# Revit family: 33-00-011-DN80-300
name_source: partatom
category: Pipe Accessories
units: mm (PartAtom-declared; Revit-internal decimal feet)

## family parameters
Always vertical = No
Cut with Voids When Loaded = No
Part Type = Valve - Breaks Into
Round Connector Dimension = Use Diameter
Shared = No
Work Plane-Based = No

## types (6) — shared parameters
Body_Wallthickness = 15 mm  [stored 0.0492126 ft]
Body_Wallthickness_ref = 8 mm  [stored 0.0262467 ft]
DN080_PN16 = 33-080-00-0147099
DN100_PN16 = 33-100-00-0147099
DN150_PN16 = 33-150-00-0147099
DN200_PN16 = 33-200-00-0147099
DN250_PN16 = 33-250-00-01770
DN300_PN16 = 33-300-00-01770
Description_ = AVK GATE VALVE WITH SOCKET ENDS
Ftc = 4 mm  [stored 0.0131234 ft]
Name_Height_reference = 10 mm  [stored 0.0328084 ft]
Rib_Thickness = 18 mm  [stored 0.0590551 ft]
Search_table = 33-00-011-DN80-300
URL product pages = https://www.avkvalves.com
zero-valued in all types: Bottom_Reference

## per-type parameters (varying)
- DN080_PN16: At=70 mm; Body_Height=130 mm; Body_depth=140 mm; Body_width=60 mm  [stored 0.19685 ft]; Bonnet_Flange_Depth=171 mm; Bonnet_Flange_Width=65 mm; Bonnet_Flange_cut=8 mm  [stored 0.0262467 ft]; Bonnet_Flange_thickness=15 mm  [stored 0.0492126 ft]; Bonnet_Height=50 mm  [stored 0.164042 ft]; Bonnet_Reference_height=120 mm; Bonnet_Thickness=61 mm; Bt=61 mm; Bt_2=54 mm  [stored 0.177165 ft]; CL _Thickness=19 mm  [stored 0.062336 ft]; CL_Height=75 mm; Cut_Reference=568 mm; D=63 mm; D1=10 mm  [stored 0.0328084 ft]; D2=34 mm  [stored 0.111549 ft]; Dd=98 mm; Dd_ref=49 mm  [stored 0.160761 ft]; F=9 mm; F1=20 mm  [stored 0.0656168 ft]; Fillet_Thickness=6 mm  [stored 0.019685 ft]; Flange_OR=100 mm; Flange_Thickness=30 mm  [stored 0.0984252 ft]; Flange_Thickness_cut=30 mm  [stored 0.0984252 ft]; Ftc_reference_height=100 mm; H=280 mm; H1=246 mm; H3=351 mm; H3_ref=71 mm; Horizontal_Flange_width=142 mm; ID=40 mm  [stored 0.131234 ft]; ID_ref=48 mm  [stored 0.15748 ft]; ID_ref_2=64 mm; L=284 mm; L_Dia=80 mm; L_ref=123 mm; Name_Reference=90 mm; Name_Width=30 mm  [stored 0.0984252 ft]; Neck_H=41 mm; Neck_T=17 mm  [stored 0.0557743 ft]; Neck_T2=15 mm  [stored 0.0492126 ft]; Nominal Diameter (DN)=80 mm; R1tv=1000 mm; R2f=15 mm  [stored 0.0492126 ft]; RF_Dia=66 mm; Rf=237 mm; Rib_Height_Reference_1=120 mm; Rib_Height_Reference_2=110 mm; Rib_Height_Reference_3=100 mm; Rib_Height_Reference_4=85 mm; Rib_Width_1=30 mm  [stored 0.0984252 ft]; Rib_Width_2=30 mm  [stored 0.0984252 ft]; Rib_Width_3=30 mm  [stored 0.0984252 ft]; Rib_depth_1=30 mm  [stored 0.0984252 ft]; Rib_depth_2=30 mm  [stored 0.0984252 ft]; Rib_depth_3=30 mm  [stored 0.0984252 ft]; Rt=333 mm
- DN100_PN16: At=83 mm; Body_Height=122 mm; Body_depth=166 mm; Body_width=65 mm; Bonnet_Flange_Depth=192 mm; Bonnet_Flange_Width=70 mm; Bonnet_Flange_cut=8 mm  [stored 0.0262467 ft]; Bonnet_Flange_thickness=15 mm  [stored 0.0492126 ft]; Bonnet_Height=55 mm  [stored 0.180446 ft]; Bonnet_Reference_height=112 mm; Bonnet_Thickness=66 mm; Bt=66 mm; Bt_2=59 mm; CL _Thickness=22 mm  [stored 0.0721785 ft]; CL_Height=88 mm; Cut_Reference=568 mm; D=63 mm; D1=10 mm  [stored 0.0328084 ft]; D2=34 mm  [stored 0.111549 ft]; Dd=118 mm; Dd_ref=59 mm; F=9 mm; F1=20 mm  [stored 0.0656168 ft]; Fillet_Thickness=6 mm  [stored 0.019685 ft]; Flange_OR=110 mm; Flange_Thickness=30 mm  [stored 0.0984252 ft]; Flange_Thickness_cut=30 mm  [stored 0.0984252 ft]; Ftc_reference_height=110 mm; H=303 mm; H1=269 mm; H3=384 mm; H3_ref=81 mm; Horizontal_Flange_width=162 mm; ID=50 mm  [stored 0.164042 ft]; ID_ref=58 mm; ID_ref_2=74 mm; L=284 mm; L_Dia=100 mm; L_ref=123 mm; Name_Reference=101 mm; Name_Width=33 mm; Neck_H=59 mm; Neck_T=20 mm  [stored 0.0656168 ft]; Neck_T2=18 mm  [stored 0.0590551 ft]; Nominal Diameter (DN)=100 mm; R1tv=1100 mm; R2f=15 mm  [stored 0.0492126 ft]; RF_Dia=78 mm; Rf=270 mm; Rib_Height_Reference_1=120 mm; Rib_Height_Reference_2=110 mm; Rib_Height_Reference_3=100 mm; Rib_Height_Reference_4=90 mm; Rib_Width_1=33 mm; Rib_Width_2=33 mm; Rib_Width_3=33 mm; Rib_depth_1=33 mm; Rib_depth_2=33 mm; Rib_depth_3=33 mm; Rt=367 mm
- DN150_PN16: At=121 mm; Body_Height=192 mm; Body_depth=242 mm; Body_width=75 mm; Bonnet_Flange_Depth=272 mm; Bonnet_Flange_Width=90 mm; Bonnet_Flange_cut=8 mm  [stored 0.0262467 ft]; Bonnet_Flange_thickness=15 mm  [stored 0.0492126 ft]; Bonnet_Height=71 mm; Bonnet_Reference_height=182 mm; Bonnet_Thickness=77 mm; Bt=77 mm; Bt_2=69 mm; CL _Thickness=24 mm  [stored 0.0787402 ft]; CL_Height=126 mm; Cut_Reference=568 mm; D=63 mm; D1=10 mm  [stored 0.0328084 ft]; D2=34 mm  [stored 0.111549 ft]; Dd=170 mm; Dd_ref=85 mm; F=9 mm; F1=20 mm  [stored 0.0656168 ft]; Fillet_Thickness=12 mm  [stored 0.0393701 ft]; Flange_OR=142 mm; Flange_Thickness=30 mm  [stored 0.0984252 ft]; Flange_Thickness_cut=34 mm  [stored 0.111549 ft]; Ftc_reference_height=142 mm; H=398 mm; H1=364 mm; H3=533 mm; H3_ref=135 mm; Horizontal_Flange_width=270 mm; ID=75 mm; ID_ref=83 mm; ID_ref_2=100 mm; L=284 mm; L_Dia=150 mm; L_ref=123 mm; Name_Reference=143 mm; Name_Width=38 mm  [stored 0.124672 ft]; Neck_H=46 mm; Neck_T=22 mm  [stored 0.0721785 ft]; Neck_T2=20 mm  [stored 0.0656168 ft]; Nominal Diameter (DN)=150 mm; R1tv=1420 mm; R2f=30 mm  [stored 0.0984252 ft]; RF_Dia=106 mm; Rf=450 mm; Rib_Height_Reference_1=120 mm; Rib_Height_Reference_2=110 mm; Rib_Height_Reference_3=100 mm; Rib_Height_Reference_4=150 mm; Rib_Width_1=38 mm  [stored 0.124672 ft]; Rib_Width_2=38 mm  [stored 0.124672 ft]; Rib_Width_3=38 mm  [stored 0.124672 ft]; Rib_depth_1=38 mm  [stored 0.124672 ft]; Rib_depth_2=38 mm  [stored 0.124672 ft]; Rib_depth_3=38 mm  [stored 0.124672 ft]; Rt=473 mm
- DN200_PN16: At=147 mm; Body_Height=245 mm; Body_depth=294 mm; Body_width=100 mm; Bonnet_Flange_Depth=332 mm; Bonnet_Flange_Width=110 mm; Bonnet_Flange_cut=13 mm; Bonnet_Flange_thickness=25 mm  [stored 0.082021 ft]; Bonnet_Height=85 mm; Bonnet_Reference_height=235 mm; Bonnet_Thickness=102 mm; Bt=102 mm; Bt_2=94 mm; CL _Thickness=30 mm  [stored 0.0984252 ft]; CL_Height=152 mm; Cut_Reference=740 mm; D=63 mm; D1=10 mm  [stored 0.0328084 ft]; D2=34 mm  [stored 0.111549 ft]; Dd=222 mm; Dd_ref=111 mm; F=9 mm; F1=20 mm  [stored 0.0656168 ft]; Fillet_Thickness=24 mm  [stored 0.0787402 ft]; Flange_OR=170 mm; Flange_Thickness=40 mm  [stored 0.131234 ft]; Flange_Thickness_cut=35 mm  [stored 0.114829 ft]; Ftc_reference_height=170 mm; H=488 mm; H1=454 mm; H3=627 mm; H3_ref=139 mm; Horizontal_Flange_width=278 mm; ID=100 mm; ID_ref=108 mm; ID_ref_2=126 mm; L=370 mm; L_Dia=200 mm; L_ref=161 mm; Name_Reference=183 mm; Name_Width=50 mm  [stored 0.164042 ft]; Neck_H=57 mm; Neck_T=28 mm; Neck_T2=26 mm; Nominal Diameter (DN)=200 mm; R1tv=1700 mm; R2f=60 mm  [stored 0.19685 ft]; RF_Dia=133 mm; Rf=463 mm; Rib_Height_Reference_1=120 mm; Rib_Height_Reference_2=110 mm; Rib_Height_Reference_3=100 mm; Rib_Height_Reference_4=180 mm; Rib_Width_1=50 mm  [stored 0.164042 ft]; Rib_Width_2=50 mm  [stored 0.164042 ft]; Rib_Width_3=50 mm  [stored 0.164042 ft]; Rib_depth_1=50 mm  [stored 0.164042 ft]; Rib_depth_2=50 mm  [stored 0.164042 ft]; Rib_depth_3=50 mm  [stored 0.164042 ft]; Rt=567 mm
- DN250_PN16: At=171 mm; Body_Height=370 mm; Body_depth=342 mm; Body_width=100 mm; Bonnet_Flange_Depth=372 mm; Bonnet_Flange_Width=130 mm; Bonnet_Flange_cut=13 mm; Bonnet_Flange_thickness=25 mm  [stored 0.082021 ft]; Bonnet_Height=100 mm; Bonnet_Reference_height=360 mm; Bonnet_Thickness=102 mm; Bt=102 mm; Bt_2=94 mm; CL _Thickness=30 mm  [stored 0.0984252 ft]; CL_Height=176 mm; Cut_Reference=780 mm; D=88 mm; D1=15 mm  [stored 0.0492126 ft]; D2=47 mm  [stored 0.154199 ft]; Dd=274 mm; Dd_ref=137 mm; F=14 mm  [stored 0.0459318 ft]; F1=31 mm  [stored 0.101706 ft]; Fillet_Thickness=24 mm  [stored 0.0787402 ft]; Flange_OR=200 mm; Flange_Thickness=44 mm  [stored 0.144357 ft]; Flange_Thickness_cut=38 mm  [stored 0.124672 ft]; Ftc_reference_height=200 mm; H=664 mm; H1=617 mm; H3=826 mm; H3_ref=162 mm; Horizontal_Flange_width=324 mm; ID=125 mm; ID_ref=133 mm; ID_ref_2=152 mm; L=390 mm; L_Dia=250 mm; L_ref=170 mm; Name_Reference=270 mm; Name_Width=50 mm  [stored 0.164042 ft]; Neck_H=71 mm; Neck_T=28 mm; Neck_T2=26 mm; Nominal Diameter (DN)=250 mm; R1tv=2000 mm; R2f=60 mm  [stored 0.19685 ft]; RF_Dia=160 mm; Rf=540 mm; Rib_Height_Reference_1=90 mm; Rib_Height_Reference_2=110 mm; Rib_Height_Reference_3=100 mm; Rib_Height_Reference_4=200 mm; Rib_Width_1=125 mm; Rib_Width_2=125 mm; Rib_Width_3=50 mm  [stored 0.164042 ft]; Rib_depth_1=372 mm; Rib_depth_2=50 mm  [stored 0.164042 ft]; Rib_depth_3=50 mm  [stored 0.164042 ft]; Rt=667 mm
- DN300_PN16: At=209 mm; Body_Height=420 mm; Body_depth=418 mm; Body_width=100 mm; Bonnet_Flange_Depth=432 mm; Bonnet_Flange_Width=140 mm; Bonnet_Flange_cut=18 mm  [stored 0.0590551 ft]; Bonnet_Flange_thickness=35 mm  [stored 0.114829 ft]; Bonnet_Height=114 mm; Bonnet_Reference_height=410 mm; Bonnet_Thickness=102 mm; Bt=102 mm; Bt_2=94 mm; CL _Thickness=30 mm  [stored 0.0984252 ft]; CL_Height=214 mm; Cut_Reference=880 mm; D=88 mm; D1=15 mm  [stored 0.0492126 ft]; D2=47 mm  [stored 0.154199 ft]; Dd=326 mm; Dd_ref=163 mm; F=14 mm  [stored 0.0459318 ft]; F1=31 mm  [stored 0.101706 ft]; Fillet_Thickness=24 mm  [stored 0.0787402 ft]; Flange_OR=228 mm; Flange_Thickness=50 mm  [stored 0.164042 ft]; Flange_Thickness_cut=39 mm  [stored 0.127953 ft]; Ftc_reference_height=228 mm; H=740 mm; H1=693 mm; H3=931 mm; H3_ref=191 mm; Horizontal_Flange_width=382 mm; ID=150 mm; ID_ref=158 mm; ID_ref_2=178 mm; L=440 mm; L_Dia=300 mm; L_ref=191 mm; Name_Reference=250 mm; Name_Width=50 mm  [stored 0.164042 ft]; Neck_H=59 mm; Neck_T=28 mm; Neck_T2=26 mm; Nominal Diameter (DN)=300 mm; R1tv=2280 mm; R2f=60 mm  [stored 0.19685 ft]; RF_Dia=185 mm; Rf=637 mm; Rib_Height_Reference_1=178 mm; Rib_Height_Reference_2=285 mm; Rib_Height_Reference_3=165 mm; Rib_Height_Reference_4=300 mm; Rib_Width_1=130 mm; Rib_Width_2=130 mm; Rib_Width_3=50 mm  [stored 0.164042 ft]; Rib_depth_1=432 mm; Rib_depth_2=432 mm; Rib_depth_3=50 mm  [stored 0.164042 ft]; Rt=760 mm

note: [stored X ft] marks values corroborated as IEEE doubles in the binary element streams (Revit-internal decimal feet)

## geometry (parser evidence)
native form markers: Extrusion x1, Sweep x2
no freeform markers — native parametric forms only
